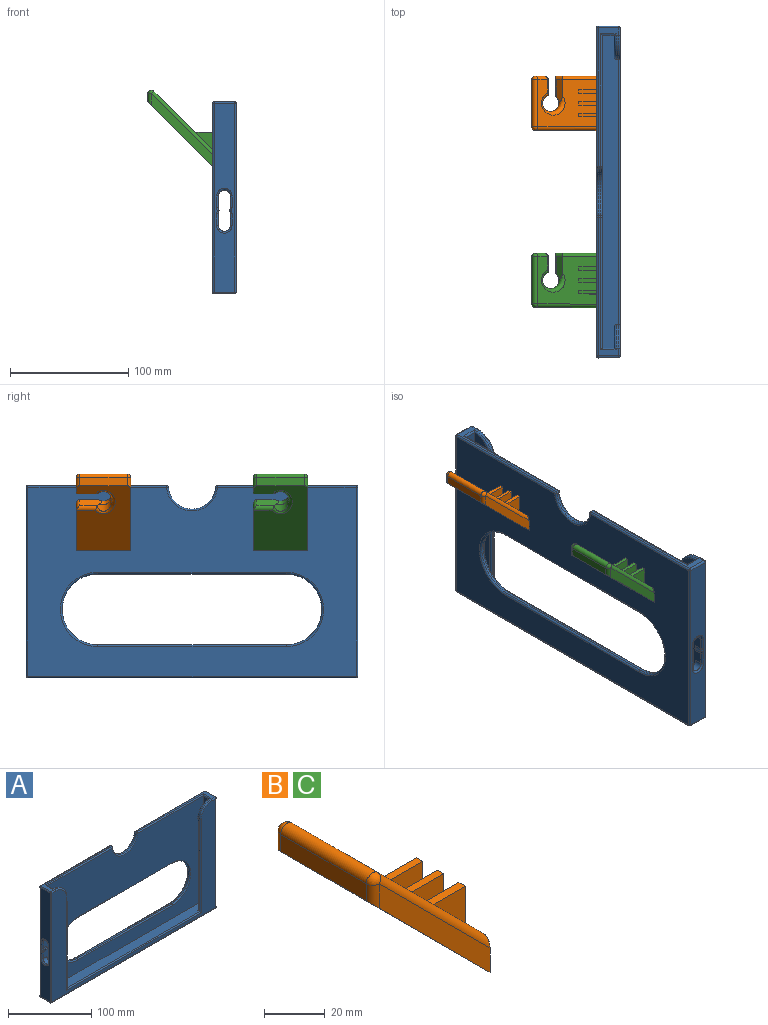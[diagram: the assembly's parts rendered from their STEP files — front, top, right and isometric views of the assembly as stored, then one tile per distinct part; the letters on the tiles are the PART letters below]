
ASSEMBLY  parts=3 mates=2
PART A: 113 faces, bbox 281x20x164.6 mm
  f0: cylinder r=5mm len=6.5mm, axis (-1,0,0), area 17mm2, adj f4,f23,f35,f40
  f1: plane 160x17mm, normal (-1,0,0), area 2263.9mm2, adj f40,f41,f42,f43,f44,f45,f46,f47
  f2: plane 5x0.67mm, normal (-1,0,0), area 1.1mm2, adj f6,f29,f38
  f3: plane 5x0.67mm, normal (-1,0,0), area 1.1mm2, adj f9,f33,f37
  f4: plane 5x0.67mm, normal (1,0,0), area 1.1mm2, adj f0,f23,f35
  f5: plane 5x0.67mm, normal (1,0,0), area 1.1mm2, adj f9,f31,f34
  f6: cylinder r=5mm len=6.5mm, axis (-1,0,0), area 17mm2, adj f2,f29,f38,f50
  f7: plane 50x10mm, normal (-1,0,0), area 460.7mm2, adj f9,f21,f29,f32
  f8: plane 50x10mm, normal (1,0,0), area 460.7mm2, adj f9,f21,f23,f30
  f9: plane 278x153.5mm, normal (0,-1,0), area 27078.6mm2, adj f3,f5,f7,f8,f20,f21,f22,f30
  f10: cylinder r=30mm len=60mm, axis (0,-1,0), area 188.5mm2, adj f11,f18,f105,f110
  f11: plane 160x2mm, normal (0,0,-1), area 320mm2, adj f10,f12,f106,f112
  f12: cylinder r=30mm len=60mm, axis (0,-1,0), area 188.5mm2, adj f11,f18,f108,f111
  f13: plane 117.55x17mm, normal (0,0,1), area 313.1mm2, adj f24,f66,f68,f71,f82,f92,f100,f104
  f14: cylinder r=20mm len=39.9mm, axis (0,-1,0), area 120.1mm2, adj f72,f73,f82,f83
  f15: plane 117.55x17mm, normal (0,0,1), area 313.1mm2, adj f27,f63,f65,f67,f73,f74,f76,f81
  f16: plane 278x17mm, normal (0,0,-1), area 4726mm2, adj f84,f85,f94,f95
  f17: plane 160x17mm, normal (1,0,0), area 2263.9mm2, adj f50,f51,f52,f53,f54,f55,f56,f57
  f18: plane 160x2mm, normal (0,0,1), area 320mm2, adj f10,f12,f107,f109
  f19: plane 278x160mm, normal (0,1,0), area 30621.1mm2, adj f74,f75,f83,f84,f92,f93,f109,f110
  f20: plane 78.5x10mm, normal (-1,0,0), area 745.7mm2, adj f9,f29,f39,f68
  f21: plane 265x13.5mm, normal (0,0,1), area 3438.5mm2, adj f7,f8,f9,f23,f25,f26,f29,f60
  f22: plane 78.5x10mm, normal (1,0,0), area 745.7mm2, adj f9,f23,f36,f65
  f23: plane 153.5x25mm, normal (0,1,0), area 2896.3mm2, adj f0,f4,f8,f21,f22,f30,f35,f36
  f24: cylinder r=20mm len=20mm, axis (0,1,0), area 62.8mm2, adj f13,f25,f64,f102
  f25: plane 135x2mm, normal (-1,0,0), area 270mm2, adj f21,f24,f62,f99
  f26: plane 135x2mm, normal (1,0,0), area 270mm2, adj f21,f27,f60,f91
  f27: cylinder r=20mm len=20mm, axis (0,1,0), area 62.8mm2, adj f15,f26,f61,f87
  f28: plane 278x160mm, normal (0,-1,0), area 8993.1mm2, adj f81,f86,f87,f91,f95,f96,f99,f101
  f29: plane 153.5x25mm, normal (0,1,0), area 2896.3mm2, adj f2,f6,f7,f20,f21,f32,f38,f39
  f30: cylinder r=5mm len=10mm, axis (-1,0,0), area 102.1mm2, adj f8,f9,f23,f44
  f31: cylinder r=5mm len=6.5mm, axis (-1,0,0), area 17mm2, adj f5,f9,f34,f48
  f32: cylinder r=5mm len=10mm, axis (-1,0,0), area 102.1mm2, adj f7,f9,f29,f54
  f33: cylinder r=5mm len=6.5mm, axis (-1,0,0), area 17mm2, adj f3,f9,f37,f58
  f34: cylinder r=5mm len=6.5mm, axis (1,0,0), area 17mm2, adj f5,f9,f31,f49
  f35: cylinder r=5mm len=6.5mm, axis (1,0,0), area 17mm2, adj f0,f4,f23,f41
  f36: cylinder r=5mm len=10mm, axis (1,0,0), area 102.1mm2, adj f9,f22,f23,f45
  f37: cylinder r=5mm len=6.5mm, axis (1,0,0), area 17mm2, adj f3,f9,f33,f59
  f38: cylinder r=5mm len=6.5mm, axis (1,0,0), area 17mm2, adj f2,f6,f29,f51
  f39: cylinder r=5mm len=10mm, axis (1,0,0), area 102.1mm2, adj f9,f20,f29,f55
  f40: torus R=6.5mm, axis (1,0,0), area 6.1mm2, adj f0,f1,f41,f42
  f41: torus R=6.5mm, axis (1,0,0), area 6.1mm2, adj f1,f35,f40,f43
  f42: cylinder r=1.5mm len=10mm, axis (0,0,1), area 23.6mm2, adj f1,f23,f40,f44
  f43: cylinder r=1.5mm len=10mm, axis (0,0,1), area 23.6mm2, adj f1,f23,f41,f45
  f44: torus R=6.5mm, axis (1,0,0), area 41mm2, adj f1,f30,f42,f46
  f45: torus R=6.5mm, axis (1,0,0), area 41mm2, adj f1,f36,f43,f47
  f46: cylinder r=1.5mm len=10mm, axis (0,0,-1), area 23.6mm2, adj f1,f9,f44,f48
  f47: cylinder r=1.5mm len=10mm, axis (0,0,-1), area 23.6mm2, adj f1,f9,f45,f49
  f48: torus R=6.5mm, axis (1,0,0), area 6.1mm2, adj f1,f31,f46,f49
  f49: torus R=6.5mm, axis (1,0,0), area 6.1mm2, adj f1,f34,f47,f48
  f50: torus R=6.5mm, axis (-1,0,0), area 6.1mm2, adj f6,f17,f51,f52
  f51: torus R=6.5mm, axis (-1,0,0), area 6.1mm2, adj f17,f38,f50,f53
  f52: cylinder r=1.5mm len=10mm, axis (0,0,1), area 23.6mm2, adj f17,f29,f50,f54
  f53: cylinder r=1.5mm len=10mm, axis (0,0,1), area 23.6mm2, adj f17,f29,f51,f55
  f54: torus R=6.5mm, axis (-1,0,0), area 41mm2, adj f17,f32,f52,f56
  f55: torus R=6.5mm, axis (-1,0,0), area 41mm2, adj f17,f39,f53,f57
  f56: cylinder r=1.5mm len=10mm, axis (0,0,-1), area 23.6mm2, adj f9,f17,f54,f58
  f57: cylinder r=1.5mm len=10mm, axis (0,0,-1), area 23.6mm2, adj f9,f17,f55,f59
  f58: torus R=6.5mm, axis (-1,0,0), area 6.1mm2, adj f17,f33,f56,f59
  f59: torus R=6.5mm, axis (-1,0,0), area 6.1mm2, adj f17,f37,f57,f58
  f60: cylinder r=1.5mm len=135mm, axis (0,0,1), area 318.1mm2, adj f21,f23,f26,f61
  f61: torus R=18.5mm, axis (0,-1,0), area 72mm2, adj f23,f27,f60,f63
  f62: cylinder r=1.5mm len=135mm, axis (0,0,-1), area 318.1mm2, adj f21,f25,f29,f64
  f63: cylinder r=1.5mm len=1.5mm, axis (1,0,0), area 1.3mm2, adj f15,f61,f65
  f64: torus R=18.5mm, axis (0,-1,0), area 72mm2, adj f24,f29,f62,f66
  f65: cylinder r=1.5mm len=13mm, axis (0,-1,0), area 26.1mm2, adj f15,f22,f63,f67
  f66: cylinder r=1.5mm len=1.5mm, axis (-1,0,0), area 1.3mm2, adj f13,f64,f68
  f67: cylinder r=1.5mm len=112.55mm, axis (-1,0,0), area 262.9mm2, adj f9,f15,f65,f69
  f68: cylinder r=1.5mm len=13mm, axis (0,1,0), area 26.1mm2, adj f13,f20,f66,f71
  f69: sphere r=1.5mm, area 3.4mm2, adj f67,f72,f73
  f70: sphere r=1.5mm, area 3.5mm2, adj f74,f75,f76
  f71: cylinder r=1.5mm len=112.55mm, axis (-1,0,0), area 262.9mm2, adj f9,f13,f68,f77
  f72: torus R=21.5mm, axis (0,-1,0), area 145.3mm2, adj f9,f14,f69,f77
  f73: cylinder r=1.5mm len=2mm, axis (0,-1,0), area 4.5mm2, adj f14,f15,f69,f78
  f74: cylinder r=1.5mm len=117.55mm, axis (1,0,0), area 277mm2, adj f15,f19,f70,f78
  f75: cylinder r=1.5mm len=160mm, axis (0,0,1), area 377mm2, adj f1,f19,f70,f79
  f76: cylinder r=1.5mm len=17mm, axis (0,-1,0), area 40.1mm2, adj f1,f15,f70,f80
  f77: sphere r=1.5mm, area 3.4mm2, adj f71,f72,f82
  f78: sphere r=1.5mm, area 3.4mm2, adj f73,f74,f83
  f79: sphere r=1.5mm, area 3.5mm2, adj f75,f84,f85
  f80: sphere r=1.5mm, area 3.5mm2, adj f76,f81,f86
  f81: cylinder r=1.5mm len=6.5mm, axis (-1,0,0), area 15.3mm2, adj f15,f28,f80,f87
  f82: cylinder r=1.5mm len=2mm, axis (0,-1,0), area 4.5mm2, adj f13,f14,f77,f88
  f83: torus R=21.5mm, axis (0,-1,0), area 145.3mm2, adj f14,f19,f78,f88
  f84: cylinder r=1.5mm len=278mm, axis (-1,0,0), area 655mm2, adj f16,f19,f79,f89
  f85: cylinder r=1.5mm len=17mm, axis (0,-1,0), area 40.1mm2, adj f1,f16,f79,f90
  f86: cylinder r=1.5mm len=160mm, axis (0,0,-1), area 377mm2, adj f1,f28,f80,f90
  f87: torus R=18.5mm, axis (0,-1,0), area 72mm2, adj f27,f28,f81,f91
  f88: sphere r=1.5mm, area 3.4mm2, adj f82,f83,f92
  f89: sphere r=1.5mm, area 3.5mm2, adj f84,f93,f94
  f90: sphere r=1.5mm, area 3.5mm2, adj f85,f86,f95
  f91: cylinder r=1.5mm len=136.5mm, axis (0,0,-1), area 319.4mm2, adj f26,f28,f87,f96
  f92: cylinder r=1.5mm len=117.55mm, axis (1,0,0), area 277mm2, adj f13,f19,f88,f97
  f93: cylinder r=1.5mm len=160mm, axis (0,0,-1), area 377mm2, adj f17,f19,f89,f97
  f94: cylinder r=1.5mm len=17mm, axis (0,-1,0), area 40.1mm2, adj f16,f17,f89,f98
  f95: cylinder r=1.5mm len=278mm, axis (1,0,0), area 655mm2, adj f16,f28,f90,f98
  f96: cylinder r=1.5mm len=228mm, axis (1,0,0), area 532.7mm2, adj f21,f28,f91,f99
  f97: sphere r=1.5mm, area 3.5mm2, adj f92,f93,f100
  f98: sphere r=1.5mm, area 3.5mm2, adj f94,f95,f101
  f99: cylinder r=1.5mm len=136.5mm, axis (0,0,1), area 319.4mm2, adj f25,f28,f96,f102
  f100: cylinder r=1.5mm len=17mm, axis (0,-1,0), area 40.1mm2, adj f13,f17,f97,f103
  f101: cylinder r=1.5mm len=160mm, axis (0,0,1), area 377mm2, adj f17,f28,f98,f103
  f102: torus R=18.5mm, axis (0,-1,0), area 72mm2, adj f24,f28,f99,f104
  f103: sphere r=1.5mm, area 3.5mm2, adj f100,f101,f104
  f104: cylinder r=1.5mm len=6.5mm, axis (-1,0,0), area 15.3mm2, adj f13,f28,f102,f103
  f105: torus R=31.5mm, axis (0,-1,0), area 226.1mm2, adj f9,f10,f106,f107
  f106: cylinder r=1.5mm len=160mm, axis (1,0,0), area 377mm2, adj f9,f11,f105,f108
  f107: cylinder r=1.5mm len=160mm, axis (-1,0,0), area 377mm2, adj f9,f18,f105,f108
  f108: torus R=31.5mm, axis (0,-1,0), area 226.1mm2, adj f9,f12,f106,f107
  f109: cylinder r=1.5mm len=160mm, axis (1,0,0), area 377mm2, adj f18,f19,f110,f111
  f110: torus R=31.5mm, axis (0,-1,0), area 226.1mm2, adj f10,f19,f109,f112
  f111: torus R=31.5mm, axis (0,-1,0), area 226.1mm2, adj f12,f19,f109,f112
  f112: cylinder r=1.5mm len=160mm, axis (-1,0,0), area 377mm2, adj f11,f19,f110,f111
PART B: 35 faces, bbox 58.2x47.3x66 mm
  f0: plane 49.7x49.7mm, normal (0.71,0,0.71), area 1981mm2, adj f3,f9,f10,f13,f15,f17,f18,f25
  f1: plane 38.89x33.94mm, normal (0,1,0), area 311.5mm2, adj f3,f4,f24,f25
  f2: plane 40x6.9mm, normal (-1,0,0), area 276mm2, adj f4,f11,f13,f14
  f3: plane 47.26x30.4mm, normal (1,0,0), area 780.1mm2, adj f0,f1,f4,f6,f10,f25,f26,f27
  f4: plane 56.08x56.08mm, normal (-0.71,0,-0.71), area 2821.9mm2, adj f1,f2,f3,f5,f6,f11,f14,f21
  f5: plane 12.93x7.98mm, normal (0,1,0), area 54.5mm2, adj f4,f14,f18,f20
  f6: plane 61.72x51.82mm, normal (0,-1,0), area 513mm2, adj f3,f4,f10,f11
  f7: cylinder r=7mm len=25.77mm, axis (0,0,-1), area 193.6mm2, adj f8,f9,f15,f17,f22,f23
  f8: plane 15.39x2.96mm, normal (0.71,0,-0.71), area 58mm2, adj f7,f17,f20,f21,f22
  f9: plane 18.79x5.14mm, normal (-0.71,0,0.71), area 119.6mm2, adj f0,f7,f15,f23,f24
  f10: cylinder r=3mm len=53.94mm, axis (0.71,0,-0.71), area 338.3mm2, adj f0,f3,f6,f12
  f11: cylinder r=3mm len=9.9mm, axis (0,0,1), area 39.6mm2, adj f2,f4,f6,f12
  f12: sphere r=3mm, area 21.2mm2, adj f10,f11,f13
  f13: cylinder r=3mm len=40mm, axis (0,1,0), area 282.7mm2, adj f0,f2,f12,f16
  f14: cylinder r=3mm len=9.9mm, axis (0,0,-1), area 39.6mm2, adj f2,f4,f5,f16
  f15: bspline ~22.11x19.99mm, area 207.8mm2, adj f0,f7,f9,f17
  f16: sphere r=3mm, area 23mm2, adj f13,f14,f18
  f17: cylinder r=3mm len=13.63mm, axis (0,1,0), area 59.3mm2, adj f0,f7,f8,f15,f19
  f18: cylinder r=3mm len=10.1mm, axis (0.71,0,-0.71), area 53.2mm2, adj f0,f5,f16,f19
  f19: sphere r=3mm, area 10.5mm2, adj f17,f18,f20
  f20: cylinder r=3mm len=7.07mm, axis (-0.71,0,-0.71), area 25.9mm2, adj f5,f8,f19,f21
  f21: cylinder r=3mm len=18.26mm, axis (0,-1,0), area 75.6mm2, adj f4,f8,f20,f22
  f22: bspline ~22.11x19.99mm, area 215.6mm2, adj f4,f7,f8,f21,f23
  f23: cylinder r=3mm len=17.98mm, axis (0,1,0), area 72.6mm2, adj f4,f7,f9,f22,f24
  f24: cylinder r=3mm len=9.19mm, axis (-0.71,0,-0.71), area 33mm2, adj f1,f9,f23,f25
  f25: cylinder r=3mm len=33.23mm, axis (0.71,0,-0.71), area 193.2mm2, adj f0,f1,f3,f24
  f26: plane 15x15mm, normal (0,1,0), area 112.5mm2, adj f0,f3,f28
  f27: plane 15x15mm, normal (0,-1,0), area 112.5mm2, adj f0,f3,f28
  f28: plane 15x3mm, normal (0,0,1), area 45mm2, adj f0,f3,f26,f27
  f29: plane 15x15mm, normal (0,1,0), area 112.5mm2, adj f0,f3,f31
  f30: plane 15x15mm, normal (0,-1,0), area 112.5mm2, adj f0,f3,f31
  f31: plane 15x3mm, normal (0,0,1), area 45mm2, adj f0,f3,f29,f30
  f32: plane 15x15mm, normal (0,1,0), area 112.5mm2, adj f0,f3,f34
  f33: plane 15x15mm, normal (0,-1,0), area 112.5mm2, adj f0,f3,f34
  f34: plane 15x3mm, normal (0,0,1), area 45mm2, adj f0,f3,f32,f33
PART C: same geometry as B
PLACE A rot(axis=(0,0,1),90deg) t=(-54.72,-24.02,-21.9)mm
PLACE B t=(-114.54,191.48,-15.01)mm
PLACE C t=(-114.54,41.48,-15.01)mm
MATE fastened A.f19 <-> C.f3  axis (-1,0,0) through (-59.72,41.48,-76.9)mm
MATE fastened B.f3 <-> A.f19  axis (1,0,0) through (-59.72,191.48,-76.9)mm
